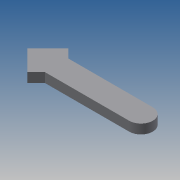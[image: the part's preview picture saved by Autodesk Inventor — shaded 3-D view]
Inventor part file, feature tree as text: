
AUTODESK INVENTOR PART (.ipt)
format: ipt  version: 2013 (Build 170138000, 138)  size: 73,728 bytes
history: native  units: mm
features: extrude x1, sketch x1
ambient origin geometry x8: Origin, YZ Plane, XZ Plane, XY Plane, X Axis, Y Axis, Z Axis, Center Point
bodies: Solid1 (feature_tree)
feature tree (2):
  extrude  "Extrusion1"  Depth=99.0mm
  sketch  "Sketch1"  dims[d0=31.0mm d1=99.0mm d2=25.0mm d3=10.0mm d4=0.0mm]
